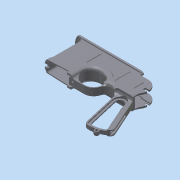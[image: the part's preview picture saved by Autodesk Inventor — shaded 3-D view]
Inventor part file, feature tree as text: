
AUTODESK INVENTOR PART (.ipt)
format: ipt  version: unknown  size: 4,652,032 bytes
history: native  units: mm
features: other x89, sketch x87, extrude x65, mirror x16, fillet x11, projected_geometry x9, revolve x8, chamfer x2, sweep x2
ambient origin geometry x8: Origin, YZ Plane, XZ Plane, XY Plane, X Axis, Y Axis, Z Axis, Center Point
feature tree (289):
  extrude  "Выдавливание1"  Depth=110.0mm
  extrude  "Выдавливание2"  Depth=59.0mm
  mirror  "Зеркальное отражение1"
  extrude  "Выдавливание3"  Depth=6.0mm
  mirror  "Зеркальное отражение2"
  extrude  "Выдавливание4"  Depth=3.0mm
  other  "НаклГрань1"
  other  "НаклГрань2"
  other  "НаклГрань3"
  extrude  "Выдавливание5"  Depth=6.0mm
  other  "НаклГрань4"
  other  "НаклГрань5"
  other  "НаклГрань6"
  extrude  "Выдавливание6"  Depth=7.0mm
  extrude  "Выдавливание7"  Depth=1.0mm
  fillet  "Сопряжение2"  Radius=3.0mm
  extrude  "Выдавливание8"  Depth=40.0mm
  fillet  "Сопряжение3"  Radius=16.0mm
  extrude  "Выдавливание9"  Depth=132.0mm
  other  "НаклГрань7"
  other  "НаклГрань8"
  fillet  "Сопряжение4"  Radius=16.0mm
  extrude  "Выдавливание10"  Depth=43.5mm
  extrude  "Выдавливание11"  Depth=19.0mm
  extrude  "Выдавливание12"  Depth=1.48353mm
  extrude  "Выдавливание13"  Depth=4.18879mm
  extrude  "Выдавливание14"  Depth=121.5mm
  extrude  "Выдавливание19"  Depth=21.0mm
  revolve  "Вращение1"
  mirror  "Зеркальное отражение9"
  extrude  "Выдавливание20"  Depth=16.0mm
  extrude  "Выдавливание21"  Depth=48.0mm
  fillet  "Сопряжение7"  Radius=32.0mm
  fillet  "Сопряжение8"  Radius=28.5mm
  extrude  "Выдавливание22"  Depth=33.0mm
  chamfer  "Фаска1"  Distance=14.0mm
  mirror  "Зеркальное отражение10"
  chamfer  "Фаска2"  Distance=8.0mm
  sketch  "Эскиз34"
  other  "РабПлоскость6"
  sweep  "Сдвиг4"
  mirror  "Зеркальное отражение11"
  extrude  "Выдавливание23"  Depth=43.0mm
  revolve  "Вращение2"
  fillet  "Сопряжение9"  Radius=101.0mm
  mirror  "Зеркальное отражение12"
  fillet  "Сопряжение10"  Radius=25.0mm
  extrude  "Выдавливание24"  Depth=1.5mm TaperAngle=0.0deg
  fillet  "Сопряжение11"  Radius=36.7mm
  extrude  "Выдавливание25"  Depth=10.0mm
  extrude  "Выдавливание26"  Depth=105.0mm
  fillet  "Сопряжение12"  Radius=6.5mm
  extrude  "Выдавливание27"  Depth=6.5mm
  extrude  "Выдавливание28"  Depth=45.0mm
  extrude  "Выдавливание29"  Depth=17.0mm
  extrude  "Выдавливание30"  Depth=17.0mm
  extrude  "Выдавливание31"  Depth=2.25mm
  extrude  "Выдавливание32"  Depth=4.5mm
  extrude  "Выдавливание33"  Depth=4.5mm
  other  "НаклГрань9"
  other  "НаклГрань10"
  extrude  "Выдавливание34"  Depth=4.5mm
  extrude  "Выдавливание35"  Depth=4.5mm
  extrude  "Выдавливание36"  Depth=3.5mm
  extrude  "Выдавливание37"  Depth=4.0mm
  extrude  "Выдавливание38"  Depth=22.0mm
  extrude  "Выдавливание39"  Depth=16.0mm
  other  "РабПлоскость7"
  extrude  "Выдавливание40"  Depth=2.25mm
  other  "РабПлоскость8"
  extrude  "Выдавливание41"  Depth=0.8mm TaperAngle=0.0deg
  extrude  "Выдавливание42"  TaperAngle=45.0deg  [1 undecoded]
  extrude  "Выдавливание43"  TaperAngle=45.0deg  [1 undecoded]
  revolve  "Вращение3"
  extrude  "Выдавливание44"  TaperAngle=45.0deg  [1 undecoded]
  extrude  "Выдавливание45"  Depth=4.0mm
  extrude  "Выдавливание46"  Depth=2.0mm
  sketch  "Эскиз63"
  other  "РабПлоскость9"
  revolve  "Вращение4"
  fillet  "Сопряжение13"  Radius=10.0mm
  revolve  "Вращение5"
  extrude  "Выдавливание47"  Depth=2.0mm
  other  "РабПлоскость18"
  other  "Разделение1"
  other  "Разделение2"
  other  "РабПлоскость19"
  other  "Разделение3"
  other  "Удаление грани1"
  other  "Сшивание поверхности1"
  other  "Разделение4"
  other  "РабПлоскость20"
  other  "Разделение5"
  other  "Удаление грани2"
  other  "Сшивание поверхности2"
  extrude  "Выдавливание48"  Depth=0.8mm TaperAngle=0.0deg
  extrude  "Выдавливание49"  TaperAngle=45.0deg  [1 undecoded]
  other  "РабПлоскость21"
  other  "Разделение6"
  other  "Разделение7"
  other  "Удаление грани3"
  other  "Разделение8"
  other  "Разделение9"
  other  "Удаление грани4"
  mirror  "Зеркальное отражение13"
  other  "Сшивание поверхности4"
  extrude  "Выдавливание50"  TaperAngle=45.0deg  [1 undecoded]
  extrude  "Выдавливание51"  TaperAngle=45.0deg  [1 undecoded]
  other  "РабПлоскость22"
  extrude  "Выдавливание52"  Depth=20.0mm
  mirror  "Зеркальное отражение14"
  extrude  "Выдавливание53"  Depth=3.0mm TaperAngle=0.0deg
  other  "НаклГрань11"
  sketch  "Эскиз82"
  other  "РабПлоскость23"
  extrude  "Выдавливание54"  Depth=3.0mm TaperAngle=0.0deg
  other  "Разделение10"
  other  "РабПлоскость24"
  mirror  "Зеркальное отражение15"
  other  "Разделение11"
  other  "Разделение12"
  mirror  "Зеркальное отражение16"
  other  "Разделение13"
  other  "Разделение14"
  other  "Удаление грани5"
  other  "Удаление грани6"
  other  "Сшивание поверхности5"
  extrude  "Выдавливание88"  Depth=4.0mm
  extrude  "Выдавливание89"  Depth=3.0mm TaperAngle=0.0deg
  mirror  "Зеркальное отражение20"
  extrude  "Выдавливание90"  Depth=4.0mm
  sketch  "Эскиз130"
  other  "РабПлоскость30"
  sketch  "Эскиз131"
  other  "РабПлоскость31"
  revolve  "Вращение9"
  extrude  "Выдавливание91"  Depth=19.5mm
  extrude  "Выдавливание92"  Depth=0.436332mm
  other  "РабПлоскость37"
  extrude  "Выдавливание104"  Depth=0.436332mm
  mirror  "Зеркальное отражение21"
  extrude  "Выдавливание95"  Depth=9.75mm
  mirror  "Зеркальное отражение22"
  other  "РабПлоскость34"
  extrude  "Выдавливание96"  Depth=54.0mm TaperAngle=0.0deg
  sweep  "Сдвиг5"
  other  "РабПлоскость35"
  extrude  "Выдавливание97"  TaperAngle=45.0deg  [1 undecoded]
  mirror  "Зеркальное отражение23"
  extrude  "Выдавливание98"  Depth=200.0mm
  mirror  "Зеркальное отражение24"
  extrude  "Выдавливание99"  Depth=46.0mm
  sketch  "Эскиз146"
  other  "РабПлоскость36"
  revolve  "Вращение10"
  fillet  "Сопряжение17"  Radius=36.0mm
  revolve  "Вращение11"
  extrude  "Выдавливание102"  Depth=3.5mm
  extrude  "Выдавливание103"  Depth=19.5mm
  mirror  "Зеркальное отражение25"
  extrude  "Выдавливание105"  Depth=10.0mm
  extrude  "Выдавливание106"  Depth=54.0mm TaperAngle=0.0deg
  sketch  "Эскиз1"
  sketch  "Эскиз2"
  sketch  "Эскиз3"
  sketch  "Эскиз4"
  sketch  "Эскиз5"
  projected_geometry  "Спроецированная петля1"
  sketch  "Эскиз6"
  sketch  "Эскиз7"
  sketch  "Эскиз8"
  sketch  "Эскиз9"
  projected_geometry  "Спроецированная петля2"
  sketch  "Эскиз10"
  sketch  "Эскиз11"
  sketch  "Эскиз12"
  sketch  "Эскиз13"
  sketch  "Эскиз14"
  sketch  "Эскиз28"
  sketch  "Эскиз29"
  projected_geometry  "Спроецированная петля4"
  sketch  "Эскиз31"
  sketch  "Эскиз32"
  sketch  "Эскиз33"
  sketch  "Эскиз35"
  sketch  "Эскиз36"
  sketch  "Эскиз38"
  sketch  "Эскиз39"
  sketch  "Эскиз40"
  sketch  "Эскиз41"
  sketch  "Эскиз42"
  sketch  "Эскиз43"
  projected_geometry  "Спроецированная петля5"
  sketch  "Эскиз44"
  sketch  "Эскиз45"
  sketch  "Эскиз46"
  projected_geometry  "Спроецированная петля6"
  sketch  "Эскиз47"
  sketch  "Эскиз48"
  sketch  "Эскиз49"
  sketch  "Эскиз50"
  sketch  "Эскиз51"
  sketch  "Эскиз52"
  sketch  "Эскиз53"
  sketch  "Эскиз54"
  sketch  "Эскиз55"
  sketch  "Эскиз56"
  sketch  "Эскиз57"
  sketch  "Эскиз58"
  sketch  "Эскиз59"
  projected_geometry  "Спроецированная петля7"
  sketch  "Эскиз60"
  sketch  "Эскиз61"
  sketch  "Эскиз62"
  sketch  "Эскиз64"
  sketch  "Эскиз65"
  sketch  "Эскиз66"
  projected_geometry  "Спроецированная петля8"
  sketch  "Эскиз73"
  sketch  "Эскиз74"
  sketch  "Эскиз75"
  sketch  "Эскиз77"
  sketch  "Эскиз78"
  sketch  "Эскиз79"
  sketch  "Эскиз80"
  sketch  "Эскиз81"
  sketch  "Эскиз83"
  sketch  "Эскиз84"
  sketch  "Эскиз85"
  sketch  "Эскиз86"
  sketch  "Эскиз125"
  sketch  "Эскиз126"
  sketch  "Эскиз127"
  sketch  "Эскиз132"
  sketch  "Эскиз133"
  sketch  "Эскиз134"
  sketch  "Эскиз138"
  sketch  "Эскиз139"
  sketch  "Эскиз140"
  sketch  "Эскиз141"
  sketch  "Эскиз142"
  sketch  "Эскиз143"
  projected_geometry  "Спроецированная петля20"
  projected_geometry  "Спроецированная петля21"
  sketch  "Эскиз144"
  sketch  "Эскиз147"
  sketch  "Эскиз148"
  sketch  "Эскиз150"
  sketch  "Эскиз151"
  sketch  "Эскиз152"
  sketch  "Эскиз153"
  sketch  "Эскиз154"
  other  "ВыдавПврх1"
  other  "ВыдавПврх2"
  other  "Участок поверхности3"
  other  "ВыдавПврх3"
  other  "ВыдавПврх4"
  other  "ВыдавПврх6"
  other  "Проецирование ребер2"
  other  "Проецирование ребер3"
  other  "Проецирование ребер4"
  other  "Проецирование ребер5"
  other  "Проецирование ребер6"
  other  "Проецирование ребер7"
  other  "Проецирование ребер8"
  other  "Проецирование ребер9"
  other  "Проецирование ребер10"
  other  "Проецирование ребер11"
  other  "Участок поверхности1"
  other  "Участок поверхности2"
  other  "Проецирование ребер17"
  other  "Участок поверхности4"
  other  "Проецирование ребер18"
  other  "Проецирование ребер19"
  other  "Проецирование ребер20"
  other  "Проецирование ребер21"
  other  "ВыдавПврх5"
  other  "ВыдавПврх7"
  other  "Участок поверхности5"
  other  "Участок поверхности6"
  other  "Проецирование ребер34"
  other  "Проецирование ребер35"
  other  "Проецирование ребер38"
  other  "Проецирование ребер40"
  other  "Проецирование ребер43"
  other  "Проецирование ребер44"
  other  "Проецирование ребер45"
  other  "Проецирование ребер46"
  other  "Проецирование ребер47"
note: 7 required parameter values undecoded (feature->parameter linkage not recoverable at this tier; creation-order binding heuristic only, values carry confidence <= 0.55)
